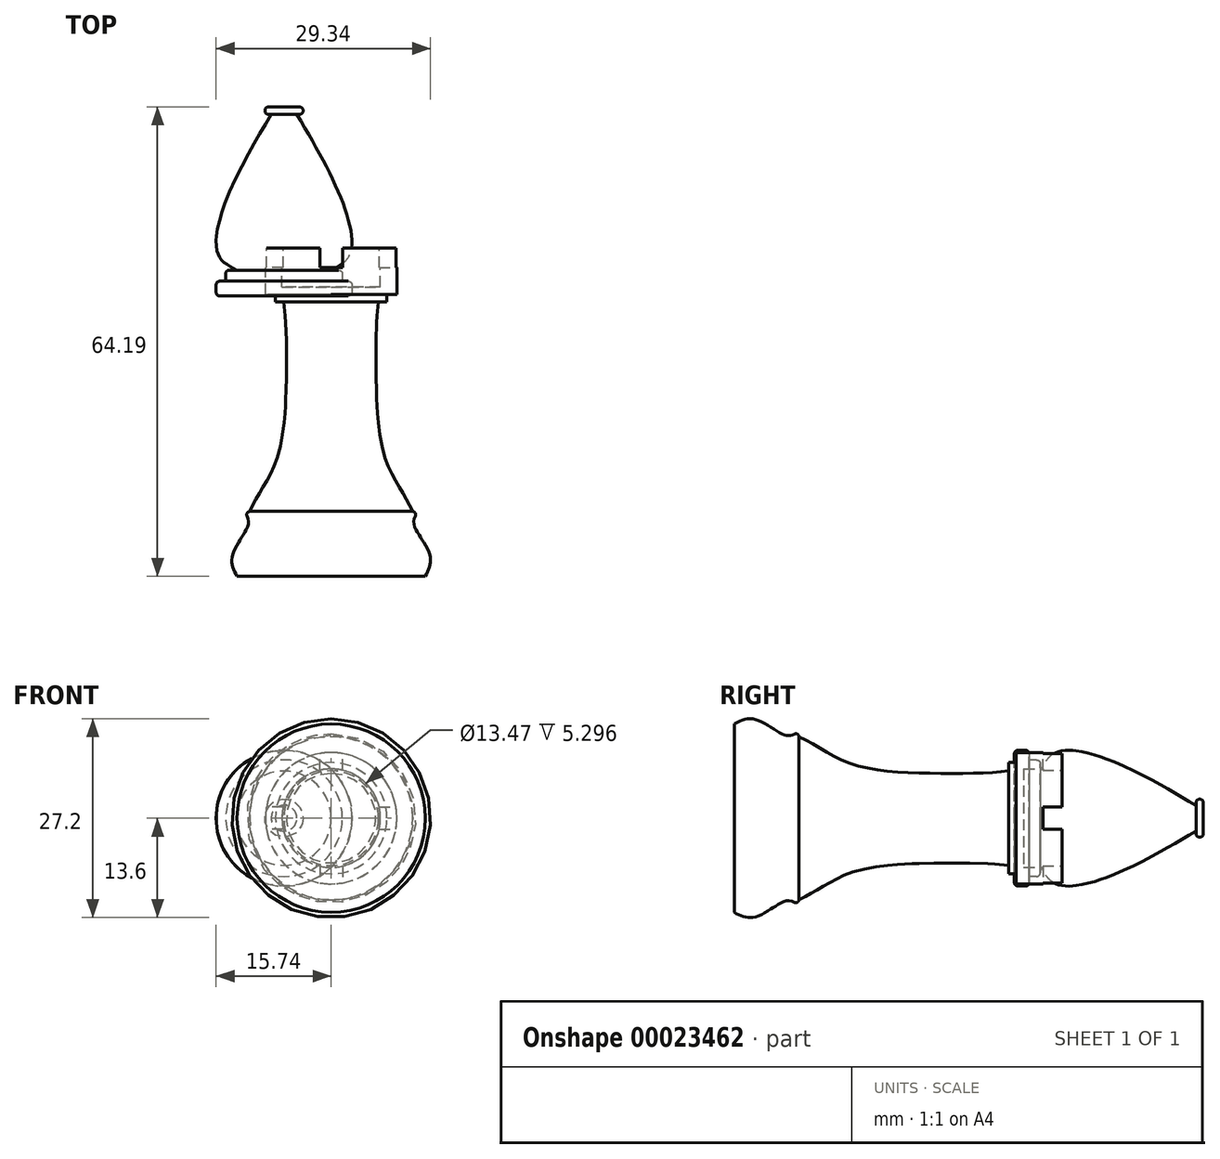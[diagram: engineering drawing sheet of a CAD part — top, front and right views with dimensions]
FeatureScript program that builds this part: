
annotation { "Feature Type Name" : "Feature", "Feature Type Description" : "" }
export const myFeature = defineFeature(function(context is Context, id is Id, definition is map)
    precondition{}
    {
        {
            var Q0;
            Q0=qCreatedBy(makeId("Top.planeOp"),FACE);
            var sketch = newSketch(context, id + "F0", { "sketchPlane" : qUnion([Q0])});
            skLineSegment(sketch, "E0", {"start": v(0, 12.94) * mm, "end": v(0, -18.8) * mm});
            skLineSegment(sketch, "E1", {"start": v(0, 12.94) * mm, "end": v(6.99, 12.94) * mm});
            skLineSegment(sketch, "E2", {"start": v(0, -13.6) * mm, "end": v(0, -14.4) * mm});
            skPoint(sketch, "E3", {"position": v(6.48, 11.92) * mm});
            skLineSegment(sketch, "E4", {"start": v(6.48, 10.9) * mm, "end": v(0, 10.9) * mm});
            skPoint(sketch, "E5.visualSharp", {"position": v(10.3, -11.3) * mm});
            skFitSpline(sketch, "E6", {"points": [v(6.48, 10.9) * mm, v(6.15, 0) * mm, v(7.64, -11.18) * mm, v(11.13, -17.78) * mm], "startDerivative": vector(-3.07, -22.33) * mm, "endDerivative": vector(9.31, -22.1) * mm});
            skPoint(sketch, "E7", {"position": v(0, 0) * mm});
            skLineSegment(sketch, "E8", {"start": v(6.48, 10.9) * mm, "end": v(7.61, 10.9) * mm});
            skLineSegment(sketch, "E9", {"start": v(7.61, 10.9) * mm, "end": v(7.61, 11.92) * mm});
            skLineSegment(sketch, "E10", {"start": v(7.61, 11.92) * mm, "end": v(0, 11.92) * mm});
            skLineSegment(sketch, "E11", {"start": v(7.61, 11.92) * mm, "end": v(8.98, 11.92) * mm});
            skLineSegment(sketch, "E12", {"start": v(8.98, 11.92) * mm, "end": v(8.98, 12.94) * mm});
            skLineSegment(sketch, "E13", {"start": v(8.98, 12.94) * mm, "end": v(6.99, 12.94) * mm});
            skLineSegment(sketch, "E14", {"start": v(8.98, 12.94) * mm, "end": v(8.98, 18.24) * mm});
            skLineSegment(sketch, "E15", {"start": v(0, 18.24) * mm, "end": v(0, 12.94) * mm});
            skLineSegment(sketch, "E16", {"start": v(6.74, 18.24) * mm, "end": v(8.98, 18.24) * mm});
            skPoint(sketch, "E17.orphan", {"position": v(4.5, 18.24) * mm});
            skLineSegment(sketch, "E18", {"start": v(6.74, 18.24) * mm, "end": v(6.74, 12.94) * mm});
            skLineSegment(sketch, "E19", {"start": v(0, -18.8) * mm, "end": v(0, -27.48) * mm});
            skLineSegment(sketch, "E20", {"start": v(11.13, -17.78) * mm, "end": v(11.13, -17.78) * mm});
            skLineSegment(sketch, "E21", {"start": v(0, -27.48) * mm, "end": v(13.28, -27.48) * mm});
            skLineSegment(sketch, "E22", {"start": v(13.28, -27.48) * mm, "end": v(13.28, -26.64) * mm});
            skLineSegment(sketch, "E23", {"start": v(0, -26.64) * mm, "end": v(13.28, -26.64) * mm});
            skFitSpline(sketch, "E24", {"points": [v(11.8, -17.78) * mm, v(11.4, -19.77) * mm, v(13.47, -23.63) * mm, v(12.88, -26.64) * mm], "startDerivative": vector(-4.7, -9.87) * mm, "endDerivative": vector(-5.55, -9.63) * mm});
            skArc(sketch, "E25.filletArc", {"start": v(11.52, -18.37) * mm, "mid": v(11.49, -17.97) * mm, "end": v(11.13, -17.78) * mm});
            skSolve(sketch);
        }
        {
            var Q0;
            Q0=makeQuery(id+"F0.imprint","IMPRINT",FACE,{"disambiguationData":[TD([[makeQuery(id+"F0.imprint","IMPRINT",EDGE,{"derivedFrom":sQuery(id+"F0.wireOp",EDGE,"E1")}),1.0]])]});
            var Q1;
            {var subQ1=sQuery(id+"F0.wireOp",EDGE,"E1");Q1=makeQuery(id+"F0.imprint","IMPRINT",FACE,{"disambiguationData":[TD([[makeQuery(id+"F0.imprint","IMPRINT",EDGE,{"derivedFrom":subQ1}),-1.0]])]});}
            var Q2;
            {var subQ1=sQuery(id+"F0.wireOp",EDGE,"E4");Q2=makeQuery(id+"F0.imprint","IMPRINT",FACE,{"disambiguationData":[TD([[makeQuery(id+"F0.imprint","IMPRINT",EDGE,{"derivedFrom":subQ1}),-1.0]])]});}
            var Q3;
            {var subQ1=sQuery(id+"F0.wireOp",EDGE,"E4");Q3=makeQuery(id+"F0.imprint","IMPRINT",FACE,{"disambiguationData":[TD([[makeQuery(id+"F0.imprint","IMPRINT",EDGE,{"derivedFrom":subQ1}),1.0]])]});}
            var Q4;
            {var subQ2=sQuery(id+"F0.wireOp",EDGE,"E2");Q4=makeQuery(id+"F0.imprint","IMPRINT",FACE,{"disambiguationData":[TD([[makeQuery(id+"F0.imprint","IMPRINT",EDGE,{"derivedFrom":subQ2}),1.0]])]});}
            var Q5;
            {var subQ1=sQuery(id+"F0.wireOp",EDGE,"704f86f3-39c6-4189-ac0f-7bc39f78269e");Q5=makeQuery(id+"F0.imprint","IMPRINT",FACE,{"disambiguationData":[TD([[makeQuery(id+"F0.imprint","IMPRINT",EDGE,{"derivedFrom":subQ1}),1.0]])]});}
            var Q6;
            Q6=sQuery(id+"F0.wireOp",EDGE,"E0");
            revolve(context, id + "F1", {"entities" : qUnion([Q0, Q1, Q2, Q3, Q4, Q5]), "axis" : qUnion([Q6]), "revolveType" : RevolveType.FULL});
        }
        {
            var Q0;
            Q0=qCreatedBy(makeId("Front.planeOp"),FACE);
            cPlane(context, id + "F2", {"entities" : qUnion([Q0]), "cplaneType" : CPlaneType.OFFSET, "offset" : 18.24 * mm, "oppositeDirection" : true, "width" : 152.4 * mm, "height" : 152.4 * mm});
        }
        {
            var Q0;
            Q0=qCreatedBy(id+"F2.planeOp",FACE);
            var sketch = newSketch(context, id + "F3", { "sketchPlane" : qUnion([Q0])});
            skCircle(sketch, "E26", {"center": v(0, 0) * mm, "radius": 8.98 * mm});
            skLineSegment(sketch, "E27", {"start": v(0, 0) * mm, "end": v(0, 1.54) * mm});
            skLineSegment(sketch, "E28", {"start": v(0, 0) * mm, "end": v(-1.54, 0) * mm});
            skLineSegment(sketch, "E29", {"start": v(0, 0) * mm, "end": v(0, -1.54) * mm});
            skLineSegment(sketch, "E30", {"start": v(0, 0) * mm, "end": v(1.54, 0) * mm});
            skLineSegment(sketch, "E31", {"start": v(0, 1.54) * mm, "end": v(8.85, 1.54) * mm});
            skLineSegment(sketch, "E32.MirrorCS", {"start": v(0, -1.54) * mm, "end": v(8.85, -1.54) * mm});
            skLineSegment(sketch, "E33.MirrorCS", {"start": v(0, 1.54) * mm, "end": v(-8.85, 1.54) * mm});
            skLineSegment(sketch, "E34.MirrorCS", {"start": v(0, -1.54) * mm, "end": v(-8.85, -1.54) * mm});
            skLineSegment(sketch, "E35", {"start": v(1.54, 1.54) * mm, "end": v(1.54, 8.85) * mm});
            skLineSegment(sketch, "E36.MirrorCS", {"start": v(-1.54, 1.54) * mm, "end": v(-1.54, 8.85) * mm});
            skLineSegment(sketch, "E37.MirrorCS", {"start": v(1.54, -1.54) * mm, "end": v(1.54, -8.85) * mm});
            skLineSegment(sketch, "E38.MirrorCS", {"start": v(-1.54, -1.54) * mm, "end": v(-1.54, -8.85) * mm});
            skLineSegment(sketch, "E39", {"start": v(1.54, 1.54) * mm, "end": v(1.54, -1.54) * mm});
            skLineSegment(sketch, "E40", {"start": v(-1.54, 1.54) * mm, "end": v(-1.54, -1.54) * mm});
            skSolve(sketch);
        }
        {
            var Q0;
            {var subQ4=sQuery(id+"F3.wireOp",EDGE,"E31");var subQ6=sQuery(id+"F3.wireOp",EDGE,"E26");var subQ8=makeQuery(id+"F3.imprint","INTERSECT",VERTEX,{"derivedFrom":[subQ6,subQ4]});Q0=makeQuery(id+"F3.imprint","IMPRINT",FACE,{"disambiguationData":[TD([[makeQuery(id+"F3.imprint","IMPRINT",EDGE,{"disambiguationData":[TD([[subQ8,1.0]])],"derivedFrom":subQ6}),1.0]])]});}
            var Q1;
            {var subQ4=sQuery(id+"F3.wireOp",EDGE,"E33.MirrorCS");var subQ6=sQuery(id+"F3.wireOp",EDGE,"E26");var subQ7=makeQuery(id+"F3.imprint","INTERSECT",VERTEX,{"derivedFrom":[subQ6,subQ4]});Q1=makeQuery(id+"F3.imprint","IMPRINT",FACE,{"disambiguationData":[TD([[makeQuery(id+"F3.imprint","IMPRINT",EDGE,{"disambiguationData":[TD([[subQ7,-1.0]])],"derivedFrom":subQ6}),1.0]])]});}
            var Q2;
            {var subQ1=sQuery(id+"F3.wireOp",EDGE,"E35");Q2=makeQuery(id+"F3.imprint","IMPRINT",FACE,{"disambiguationData":[TD([[makeQuery(id+"F3.imprint","IMPRINT",EDGE,{"derivedFrom":subQ1}),1.0]])]});}
            var Q3;
            {var subQ1=sQuery(id+"F3.wireOp",EDGE,"E37.MirrorCS");Q3=makeQuery(id+"F3.imprint","IMPRINT",FACE,{"disambiguationData":[TD([[makeQuery(id+"F3.imprint","IMPRINT",EDGE,{"derivedFrom":subQ1}),-1.0]])]});}
            extrude(context, id + "F4", {"entities" : qUnion([Q0, Q1, Q2, Q3]), "operationType" : NewBodyOperationType.REMOVE, "depth" : 2.65 * mm});
        }
        {
            var Q0;
            Q0=qCreatedBy(makeId("Top.planeOp"),FACE);
            var sketch = newSketch(context, id + "F5", { "sketchPlane" : qUnion([Q0])});
            skLineSegment(sketch, "E41", {"start": v(-6.45, 13.72) * mm, "end": v(-6.45, -18.03) * mm});
            skLineSegment(sketch, "E42", {"start": v(-6.45, -12.83) * mm, "end": v(-6.45, -13.62) * mm});
            skPoint(sketch, "E43", {"position": v(0.2, 12.7) * mm});
            skLineSegment(sketch, "E44", {"start": v(0.2, 11.69) * mm, "end": v(-6.45, 11.69) * mm});
            skPoint(sketch, "E45.visualSharp", {"position": v(4, -10.52) * mm});
            skFitSpline(sketch, "E46", {"points": [v(0.2, 11.69) * mm, v(-0.13, 0.78) * mm, v(1.36, -10.4) * mm, v(4.85, -17) * mm], "startDerivative": vector(-3.07, -22.33) * mm, "endDerivative": vector(9.31, -22.1) * mm});
            skPoint(sketch, "E47", {"position": v(-6.28, 0.78) * mm});
            skLineSegment(sketch, "E48", {"start": v(0.2, 11.69) * mm, "end": v(1.33, 11.69) * mm});
            skLineSegment(sketch, "E49", {"start": v(-6.45, 19.02) * mm, "end": v(-6.45, 13.72) * mm});
            skPoint(sketch, "E50.orphan", {"position": v(-1.96, 19.02) * mm});
            skLineSegment(sketch, "E51", {"start": v(-6.45, -18.03) * mm, "end": v(-6.45, -26.7) * mm});
            skLineSegment(sketch, "E52", {"start": v(4.85, -17) * mm, "end": v(4.85, -17) * mm});
            skLineSegment(sketch, "E53", {"start": v(-6.45, -26.7) * mm, "end": v(7, -26.7) * mm});
            skLineSegment(sketch, "E54", {"start": v(7, -26.7) * mm, "end": v(7, -25.85) * mm});
            skLineSegment(sketch, "E55", {"start": v(-6.45, -25.85) * mm, "end": v(7, -25.85) * mm});
            skFitSpline(sketch, "E56", {"points": [v(5.51, -17) * mm, v(5.1, -18.99) * mm, v(7.18, -22.85) * mm, v(6.6, -25.85) * mm], "startDerivative": vector(-4.7, -9.87) * mm, "endDerivative": vector(-5.55, -9.63) * mm});
            skArc(sketch, "E57.filletArc", {"start": v(5.24, -17.6) * mm, "mid": v(5.2, -17.2) * mm, "end": v(4.85, -17) * mm});
            skPoint(sketch, "E58.end.orphan", {"position": v(2.53, 19.02) * mm});
            skPoint(sketch, "E59.start.orphan", {"position": v(2.7, 13.72) * mm});
            skPoint(sketch, "E60.end.orphan", {"position": v(0.7, 13.72) * mm});
            skPoint(sketch, "E61.start.orphan", {"position": v(1.33, 12.7) * mm});
            skLineSegment(sketch, "E62", {"start": v(-6.45, 19.02) * mm, "end": v(-6.45, 30.2) * mm});
            skPoint(sketch, "E63.orphan", {"position": v(5.23, 15.1) * mm});
            skLineSegment(sketch, "E64", {"start": v(-6.45, 30.2) * mm, "end": v(-6.45, 36.54) * mm});
            skLineSegment(sketch, "E65", {"start": v(-1.97, 34.17) * mm, "end": v(-1.97, 34.17) * mm});
            skPoint(sketch, "E66.visualSharp", {"position": v(-1.97, 34.82) * mm});
            skPoint(sketch, "E67.visualSharp", {"position": v(-1.97, 33.52) * mm});
            skLineSegment(sketch, "E68", {"start": v(1.33, 11.69) * mm, "end": v(2.33, 11.69) * mm});
            skLineSegment(sketch, "E69", {"start": v(2.84, 12.2) * mm, "end": v(2.84, 13.21) * mm});
            skLineSegment(sketch, "E70", {"start": v(2.33, 13.72) * mm, "end": v(-6.45, 13.72) * mm});
            skLineSegment(sketch, "E71", {"start": v(1.53, 13.72) * mm, "end": v(1.53, 14.73) * mm});
            skLineSegment(sketch, "E72", {"start": v(1.02, 15.23) * mm, "end": v(-6.45, 15.23) * mm});
            skFitSpline(sketch, "E73", {"points": [v(0, 15.23) * mm, v(2.53, 17.34) * mm, v(1.53, 24.6) * mm, v(-6.45, 39.46) * mm], "startDerivative": vector(14.71, 7.54) * mm, "endDerivative": vector(-19.65, 32.55) * mm});
            skLineSegment(sketch, "E74", {"start": v(-6.45, 36.54) * mm, "end": v(-6.45, 37.55) * mm});
            skLineSegment(sketch, "E75", {"start": v(-6.45, 36.54) * mm, "end": v(-4.34, 36.54) * mm});
            skLineSegment(sketch, "E76", {"start": v(-3.84, 37.05) * mm, "end": v(-3.84, 37.05) * mm});
            skLineSegment(sketch, "E77", {"start": v(-4.34, 37.55) * mm, "end": v(-6.45, 37.55) * mm});
            skPoint(sketch, "E78.visualSharp", {"position": v(-3.84, 37.55) * mm});
            skArc(sketch, "E78.filletArc", {"start": v(-3.84, 37.05) * mm, "mid": v(-3.99, 37.4) * mm, "end": v(-4.34, 37.55) * mm});
            skPoint(sketch, "E79.visualSharp", {"position": v(-3.84, 36.54) * mm});
            skArc(sketch, "E79.filletArc", {"start": v(-4.34, 36.54) * mm, "mid": v(-3.99, 36.69) * mm, "end": v(-3.84, 37.05) * mm});
            skPoint(sketch, "E80.visualSharp", {"position": v(2.84, 13.72) * mm});
            skArc(sketch, "E80.filletArc", {"start": v(2.84, 13.21) * mm, "mid": v(2.69, 13.57) * mm, "end": v(2.33, 13.72) * mm});
            skPoint(sketch, "E81.visualSharp", {"position": v(2.84, 11.69) * mm});
            skArc(sketch, "E81.filletArc", {"start": v(2.33, 11.69) * mm, "mid": v(2.69, 11.84) * mm, "end": v(2.84, 12.2) * mm});
            skPoint(sketch, "E82.visualSharp", {"position": v(1.53, 15.23) * mm});
            skArc(sketch, "E82.filletArc", {"start": v(1.53, 14.73) * mm, "mid": v(1.38, 15.09) * mm, "end": v(1.02, 15.23) * mm});
            skSolve(sketch);
        }
        {
            var Q0;
            {var subQ8=sQuery(id+"F5.wireOp",EDGE,"E62");Q0=makeQuery(id+"F5.imprint","IMPRINT",FACE,{"disambiguationData":[TD([[makeQuery(id+"F5.imprint","IMPRINT",EDGE,{"derivedFrom":subQ8}),-1.0]])]});}
            var Q1;
            {var subQ4=sQuery(id+"F5.wireOp",EDGE,"E71");Q1=makeQuery(id+"F5.imprint","IMPRINT",FACE,{"disambiguationData":[TD([[makeQuery(id+"F5.imprint","IMPRINT",EDGE,{"derivedFrom":subQ4}),1.0]])]});}
            var Q2;
            {var subQ5=sQuery(id+"F5.wireOp",EDGE,"E44");Q2=makeQuery(id+"F5.imprint","IMPRINT",FACE,{"disambiguationData":[TD([[makeQuery(id+"F5.imprint","IMPRINT",EDGE,{"derivedFrom":subQ5}),-1.0]])]});}
            var Q3;
            {var subQ1=sQuery(id+"F5.wireOp",EDGE,"E74");Q3=makeQuery(id+"F5.imprint","IMPRINT",FACE,{"disambiguationData":[TD([[makeQuery(id+"F5.imprint","IMPRINT",EDGE,{"derivedFrom":subQ1}),-1.0]])]});}
            var Q4;
            {var subQ7=sQuery(id+"F5.wireOp",EDGE,"E42");Q4=makeQuery(id+"F5.imprint","IMPRINT",FACE,{"disambiguationData":[TD([[makeQuery(id+"F5.imprint","IMPRINT",EDGE,{"derivedFrom":subQ7}),1.0]])]});}
            var Q5;
            {var subQ1=sQuery(id+"F5.wireOp",EDGE,"E78.filletArc");Q5=makeQuery(id+"F5.imprint","IMPRINT",FACE,{"disambiguationData":[TD([[makeQuery(id+"F5.imprint","IMPRINT",EDGE,{"derivedFrom":subQ1}),1.0]])]});}
            var Q6;
            Q6=sQuery(id+"F5.wireOp",EDGE,"E62");
            revolve(context, id + "F6", {"entities" : qUnion([Q0, Q1, Q2, Q3, Q4, Q5]), "axis" : qUnion([Q6]), "revolveType" : RevolveType.FULL});
        }
    });
